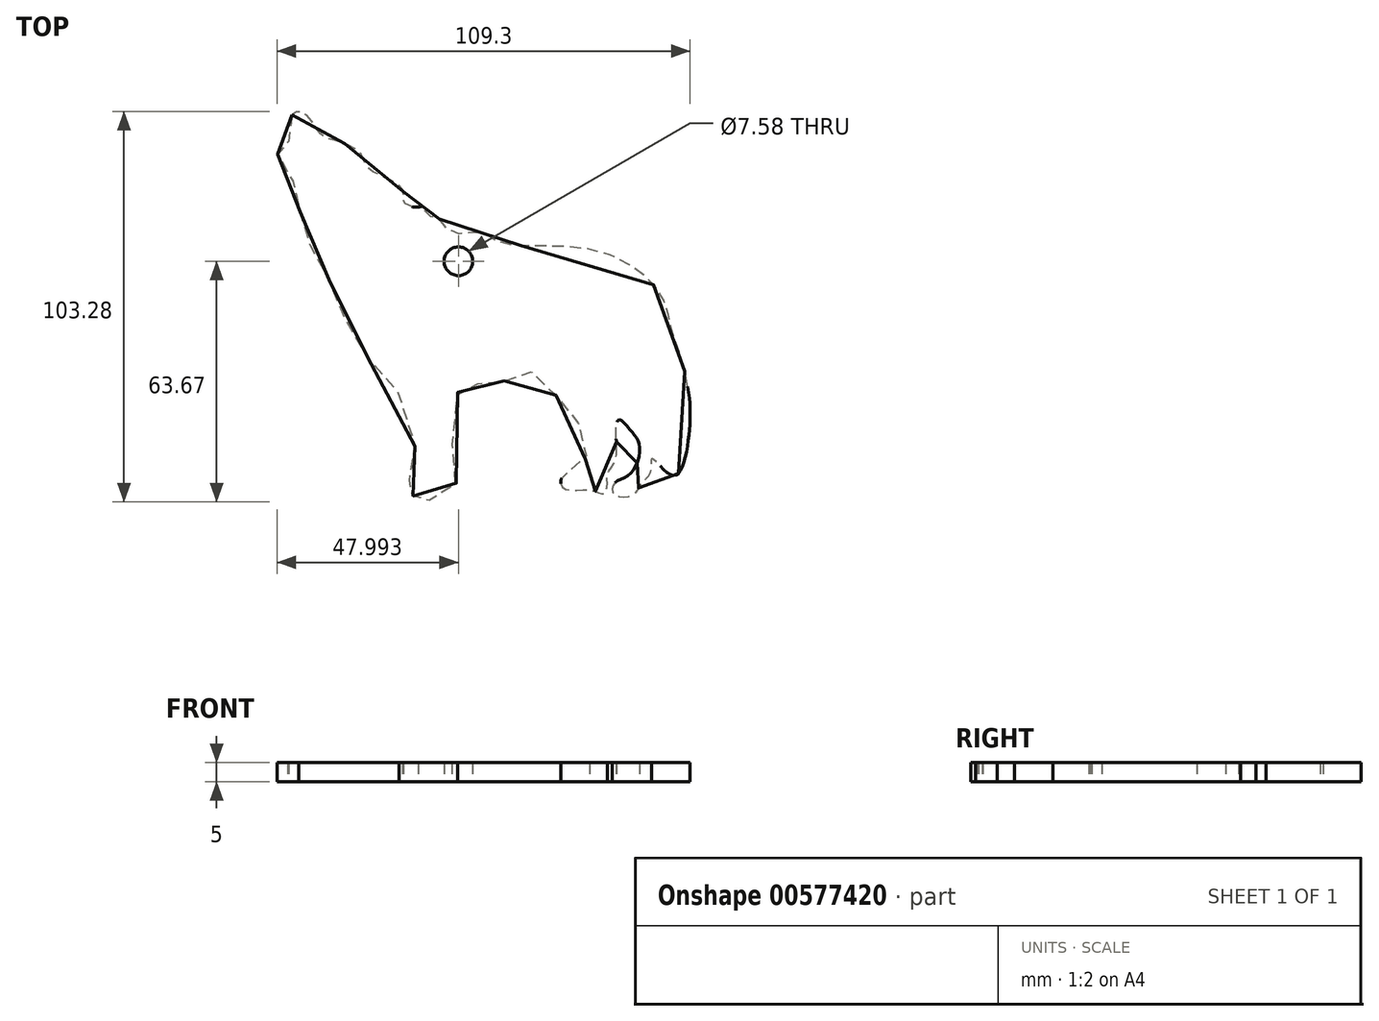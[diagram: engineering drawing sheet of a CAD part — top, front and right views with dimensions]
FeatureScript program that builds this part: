
annotation { "Feature Type Name" : "Feature", "Feature Type Description" : "" }
export const myFeature = defineFeature(function(context is Context, id is Id, definition is map)
    precondition{}
    {
        {
            var Q0;
            Q0=qCreatedBy(makeId("Top.planeOp"),FACE);
            var sketch = newSketch(context, id + "F0", { "sketchPlane" : qUnion([Q0])});
            skFitSpline(sketch, "E0", {"points": [v(-75.27, 54.13) * mm, v(-76.3, 52.26) * mm, v(-76.3, 49.98) * mm, v(-76.52, 45.2) * mm, v(-77.35, 44.17) * mm, v(-77.97, 45) * mm, v(-79.21, 43.13) * mm, v(-77.97, 39.81) * mm, v(-75.06, 36.5) * mm, v(-73.61, 34.83) * mm, v(-73.4, 29.86) * mm, v(-71.95, 24.67) * mm, v(-70.7, 20.1) * mm, v(-68.84, 15.75) * mm, v(-65.52, 10.56) * mm, v(-63.24, 5.37) * mm, v(-60.54, -2.1) * mm, v(-56.4, -9.15) * mm, v(-50.58, -13.3) * mm, v(-45.4, -24.7) * mm, v(-42.5, -34.46) * mm, v(-42.28, -40.27) * mm, v(-46.02, -44.21) * mm, v(-46.85, -46.29) * mm, v(-43.53, -46.5) * mm, v(-42.08, -48.3) * mm, v(-40.21, -46.5) * mm, v(-38.34, -48.3) * mm, v(-33.78, -43.8) * mm, v(-31.91, -43.38) * mm, v(-31.7, -39.65) * mm, v(-32.95, -30.31) * mm, v(-31.5, -20.56) * mm, v(-31.08, -17.24) * mm, v(-27.55, -17.03) * mm, v(-25.06, -16.83) * mm, v(-23.2, -16.2) * mm, v(-19.88, -16.62) * mm, v(-18.01, -15.58) * mm, v(-14.28, -14.75) * mm, v(-10.33, -13.71) * mm, v(-8.05, -17.65) * mm, v(-4.11, -21.18) * mm, v(-1, -25.95) * mm, v(3.36, -30.93) * mm, v(2.74, -35.08) * mm, v(0.87, -39.85) * mm, v(-3.7, -41.72) * mm, v(-3.49, -44.63) * mm, v(3.98, -45.25) * mm, v(7.3, -46.08) * mm, v(8.13, -43.17) * mm, v(8.13, -40.9) * mm, v(10.2, -37.36) * mm, v(10.41, -29.9) * mm, v(11.24, -26.58) * mm, v(14.35, -29.48) * mm, v(16.64, -33.42) * mm, v(14.35, -40.68) * mm, v(10, -43.38) * mm, v(10, -46.29) * mm, v(15.18, -46.29) * mm, v(16.84, -43.8) * mm, v(19.75, -40.06) * mm, v(19.96, -36.74) * mm, v(24.1, -40.68) * mm, v(27, -40.68) * mm, v(29.5, -32.18) * mm, v(29.91, -21.8) * mm, v(27.63, -10.19) * mm, v(25.35, -3.55) * mm, v(23.48, 4.13) * mm, v(17.67, 11.8) * mm, v(1.7, 18.86) * mm, v(-20.3, 20.31) * mm, v(-25.27, 23) * mm, v(-32.95, 23) * mm, v(-36.9, 26.95) * mm, v(-39.38, 27.37) * mm, v(-40.42, 29.65) * mm, v(-42.7, 29.65) * mm, v(-46.02, 31.52) * mm, v(-45.81, 33.8) * mm, v(-48.92, 36.7) * mm, v(-55.36, 40.23) * mm, v(-57.43, 44.17) * mm, v(-63.86, 47.28) * mm, v(-67.18, 48.53) * mm, v(-70.09, 52.47) * mm, v(-73.2, 54.96) * mm, v(-75.27, 54.13) * mm]});
            skCircle(sketch, "E1", {"center": v(-31.26, 15.37) * mm, "radius": 3.8 * mm});
            skSolve(sketch);
        }
        {
            var Q0;
            Q0 = qSketchRegion(id + "F0", true);
            extrude(context, id + "F1", {"entities" : qUnion([Q0]), "depth" : 5 * mm, "offsetDistance" : 25 * mm});
        }
    });
